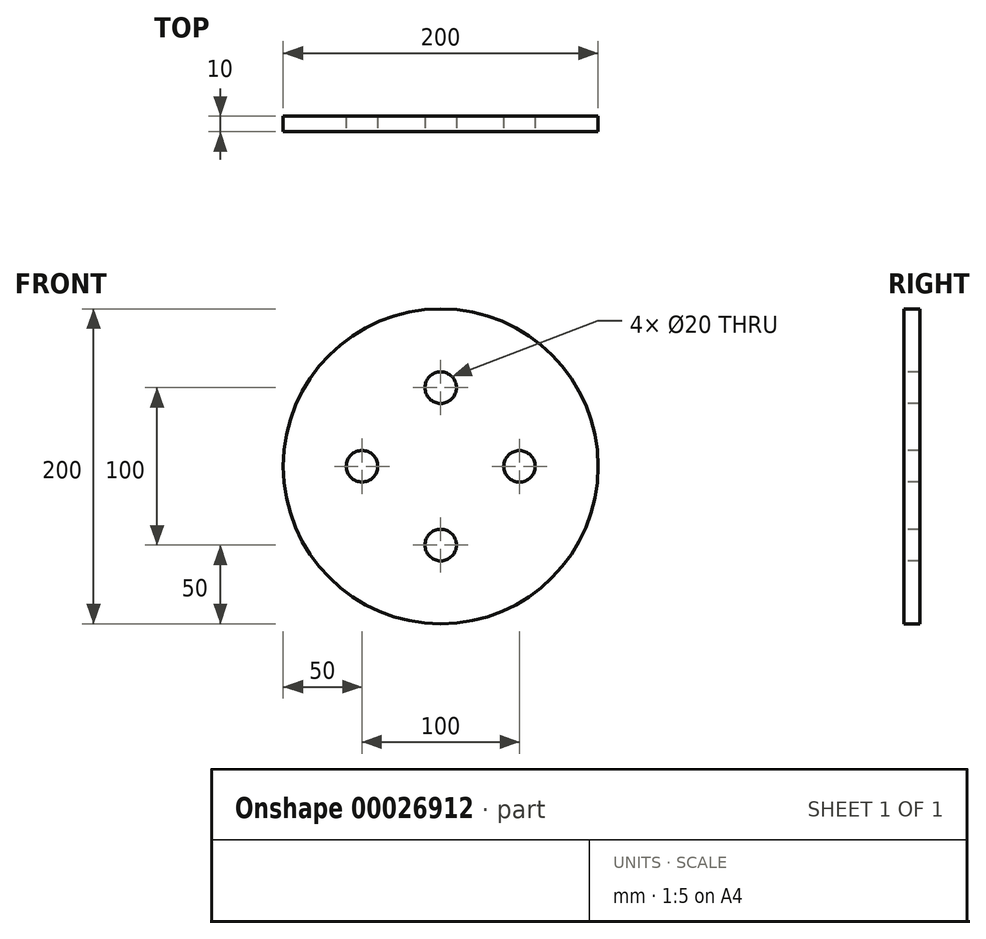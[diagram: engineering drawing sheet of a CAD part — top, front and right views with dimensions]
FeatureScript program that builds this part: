
annotation { "Feature Type Name" : "Feature", "Feature Type Description" : "" }
export const myFeature = defineFeature(function(context is Context, id is Id, definition is map)
    precondition{}
    {
        {
            var Q0;
            Q0=qCreatedBy(makeId("Front.planeOp"),FACE);
            var sketch = newSketch(context, id + "F0", { "sketchPlane" : qUnion([Q0])});
            skCircle(sketch, "E0", {"center": v(0, 0) * mm, "radius": 100 * mm});
            skSolve(sketch);
        }
        {
            var Q0;
            Q0=qSketchRegion(id+"F0",true);
            extrude(context, id + "F1", {"entities" : qUnion([Q0]), "depth" : 10 * mm});
        }
        {
            var Q0;
            Q0=makeQuery(id+"F1.opExtrude","CAP_FACE",FACE,{"disambiguationData":[OSD([sQuery(id+"F0.wireOp",EDGE,"E0")])],"isStart":false});
            var sketch = newSketch(context, id + "F2", { "sketchPlane" : qUnion([Q0])});
            skCircle(sketch, "E1", {"center": v(0, 50) * mm, "radius": 10 * mm});
            skCircle(sketch, "E2", {"center": v(50, 0) * mm, "radius": 10 * mm});
            skCircle(sketch, "E3", {"center": v(0, -50) * mm, "radius": 10 * mm});
            skCircle(sketch, "E4", {"center": v(-50, 0.06) * mm, "radius": 10 * mm});
            skSolve(sketch);
        }
        {
            var Q0;
            Q0 = qSketchRegion(id + "F2", true);
            extrude(context, id + "F3", {"entities" : qUnion([Q0]), "operationType" : NewBodyOperationType.REMOVE, "oppositeDirection" : true, "depth" : 25 * mm});
        }
    });
